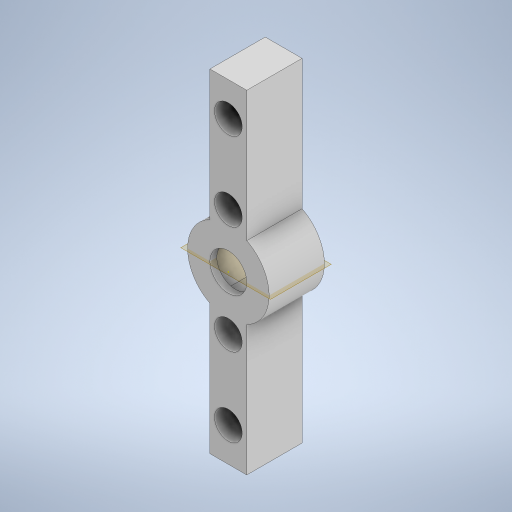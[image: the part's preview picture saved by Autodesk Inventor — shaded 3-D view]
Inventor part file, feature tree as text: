
AUTODESK INVENTOR PART (.ipt)
format: ipt  version: 2024 (Build 280153000, 153)  size: 429,056 bytes
history: native  units: in
note: dims shown in document units (in); Inventor stores cm internally (conversion verified against a paired STEP export)
features: sketch x18, extrude x16, projected_geometry x7, thread x1
ambient origin geometry x8: Origin, YZ Plane, XZ Plane, XY Plane, X Axis, Y Axis, Z Axis, Center Point
bodies: Solid1 (feature_tree)
feature tree (42):
  extrude  "Extrusion1"  Depth=0.2344in
  thread  "Thread1"  [1 undecoded]
  extrude  "Extrusion2"  Depth=0.4375in TaperAngle=0.0deg
  sketch  "Sketch3"  dims[d9=1.5in d10=0.6in]
  extrude  "Extrusion3"  Depth=0.6in
  extrude  "Extrusion4"  Depth=0.625in TaperAngle=0.0deg
  extrude  "Extrusion5"  Depth=0.25in TaperAngle=0.0deg
  extrude  "Extrusion6"  Depth=0.125in TaperAngle=0.0deg
  extrude  "Extrusion7"  Depth=0.1875in
  extrude  "Extrusion8"  Depth=0.1875in TaperAngle=0.0deg
  extrude  "Extrusion9"  Depth=0.1875in
  sketch  "Sketch10"  dims[d33=0.15in d34=0.1875in]
  extrude  "Extrusion10"  Depth=0.1875in
  sketch  "Sketch12"  dims[d38=1.8125in d39=0.0in d40=0.1875in d41=0.0in]
  extrude  "Extrusion11"  Depth=1.8125in TaperAngle=0.0deg
  extrude  "Extrusion12"  Depth=0.1875in TaperAngle=0.0deg
  extrude  "Extrusion13"  Depth=0.38in TaperAngle=0.0deg
  sketch  "Sketch15"  dims[d49=0.1875in d50=0.9in]
  extrude  "Extrusion14"  Depth=0.1875in
  extrude  "Extrusion15"  Depth=0.1875in
  extrude  "Extrusion16"  Depth=0.745in TaperAngle=0.0deg
  sketch  "Sketch1"  dims[d0=0.25in d1=0.5in d2=0.2344in d3=0.0in]
  sketch  "Sketch2"  dims[d4=0.234in d5=0.0in d6=0.4375in d7=0.0in]
  sketch  "Sketch4"  dims[d11=0.6in d12=0.625in d13=0.0in]
  projected_geometry  "Projected Loop1"
  sketch  "Sketch5"  dims[d14=0.25in d15=0.0in d16=0.8125in d17=0.0in]
  projected_geometry  "Projected Loop2"
  sketch  "Sketch6"  dims[d18=3.625in d19=0.0in d20=0.125in d21=0.0in]
  projected_geometry  "Projected Loop3"
  sketch  "Sketch7"  dims[d22=0.1875in d23=0.1875in]
  projected_geometry  "Projected Loop4"
  sketch  "Sketch8"  dims[d24=0.1875in d25=1.625in d26=0.0in]
  sketch  "Sketch9"  dims[d27=0.333in d28=0.0in d32=0.1875in]
  sketch  "Sketch11"  dims[d35=0.15in d36=1.8125in d37=0.0in]
  sketch  "Sketch13"  dims[d42=2.0in d43=0.0in d44=0.38in d45=0.0in]
  sketch  "Sketch14"  dims[d46=0.38in d47=0.0in d48=0.1875in]
  sketch  "Sketch16"  dims[d51=0.9in d52=0.745in d53=0.0in]
  projected_geometry  "Projected Loop5"
  projected_geometry  "Projected Loop6"
  sketch  "Sketch17"  dims[d29=0.5in]
  projected_geometry  "Projected Loop7"
  sketch  "Sketch18"  dims[d30=0.0344in]
note: 1 required parameter value undecoded (feature->parameter linkage not recoverable at this tier; creation-order binding heuristic only, values carry confidence <= 0.55)
